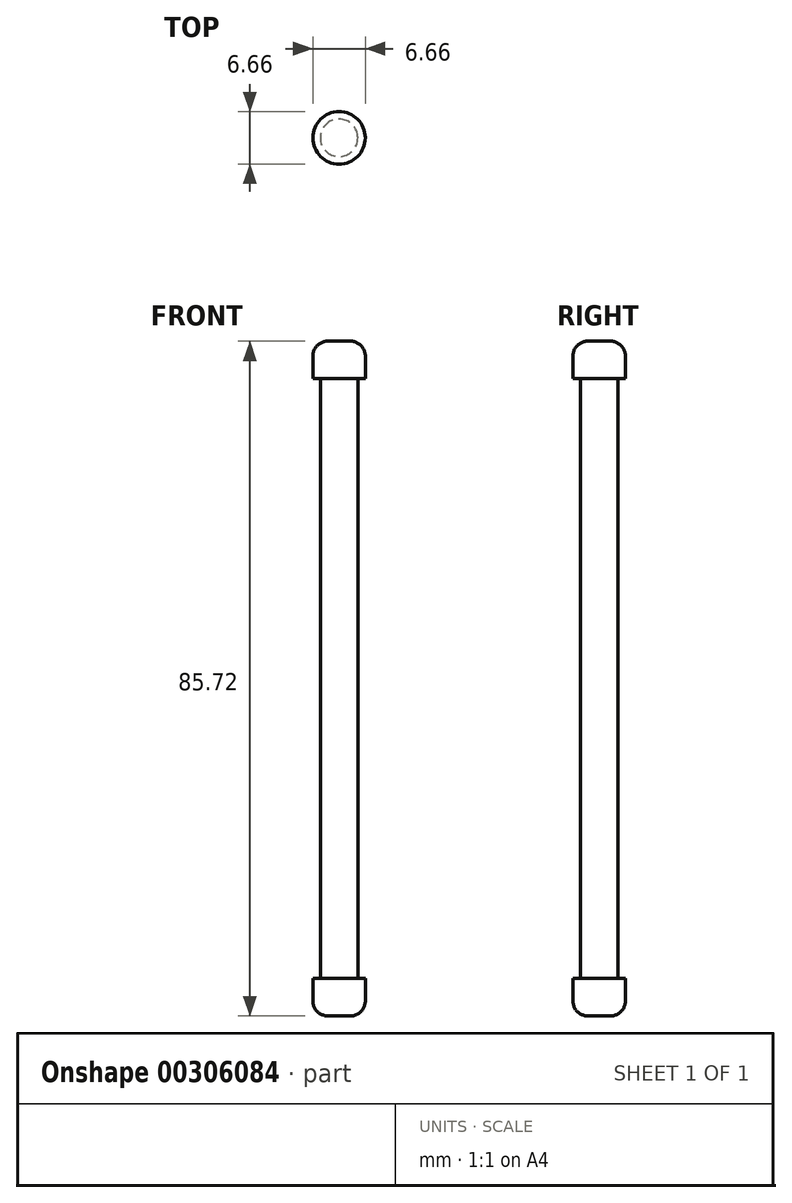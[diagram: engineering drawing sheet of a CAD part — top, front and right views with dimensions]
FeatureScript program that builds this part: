
annotation { "Feature Type Name" : "Feature", "Feature Type Description" : "" }
export const myFeature = defineFeature(function(context is Context, id is Id, definition is map)
    precondition{}
    {
        {
            var Q0;
            Q0=qCreatedBy(makeId("Top.planeOp"),FACE);
            var sketch = newSketch(context, id + "F0", { "sketchPlane" : qUnion([Q0])});
            skCircle(sketch, "E0", {"center": v(0, 0) * mm, "radius": 3.33 * mm});
            skSolve(sketch);
        }
        {
            var Q0;
            Q0 = qSketchRegion(id + "F0", true);
            extrude(context, id + "F1", {"entities" : qUnion([Q0]), "depth" : 4.76 * mm});
        }
        {
            var Q0;
            Q0=makeQuery(id+"F1.opExtrude","CAP_FACE",FACE,{"disambiguationData":[OSD([sQuery(id+"F0.wireOp",EDGE,"E0")])],"isStart":true});
            var sketch = newSketch(context, id + "F2", { "sketchPlane" : qUnion([Q0])});
            skCircle(sketch, "E1", {"center": v(0, 0) * mm, "radius": 2.38 * mm});
            skSolve(sketch);
        }
        {
            var Q0;
            Q0 = qSketchRegion(id + "F2", true);
            extrude(context, id + "F3", {"entities" : qUnion([Q0]), "operationType" : NewBodyOperationType.ADD, "depth" : 76.2 * mm});
        }
        {
            var Q0;
            Q0=makeQuery(id+"F3.opExtrude","CAP_FACE",FACE,{"disambiguationData":[OSD([sQuery(id+"F2.wireOp",EDGE,"E1")])],"isStart":false});
            var sketch = newSketch(context, id + "F4", { "sketchPlane" : qUnion([Q0])});
            skCircle(sketch, "E2", {"center": v(0, 0) * mm, "radius": 3.33 * mm});
            skSolve(sketch);
        }
        {
            var Q0;
            Q0 = qSketchRegion(id + "F4", true);
            extrude(context, id + "F5", {"entities" : qUnion([Q0]), "operationType" : NewBodyOperationType.ADD, "depth" : 4.76 * mm});
        }
        {
            var Q0;
            Q0=makeQuery(id+"F1.opExtrude","CAP_EDGE",EDGE,{"disambiguationData":[OSD([sQuery(id+"F0.wireOp",EDGE,"E0")])],"isStart":false});
            var Q1;
            Q1=makeQuery(id+"F5.opExtrude","CAP_EDGE",EDGE,{"disambiguationData":[OSD([sQuery(id+"F4.wireOp",EDGE,"E2")])],"isStart":false});
            fillet(context, id + "F6", {"entities" : qUnion([Q0, Q1]), "radius" : 1.9 * mm, "tangentPropagation" : true, "allowEdgeOverflow" : false});
        }
    });
